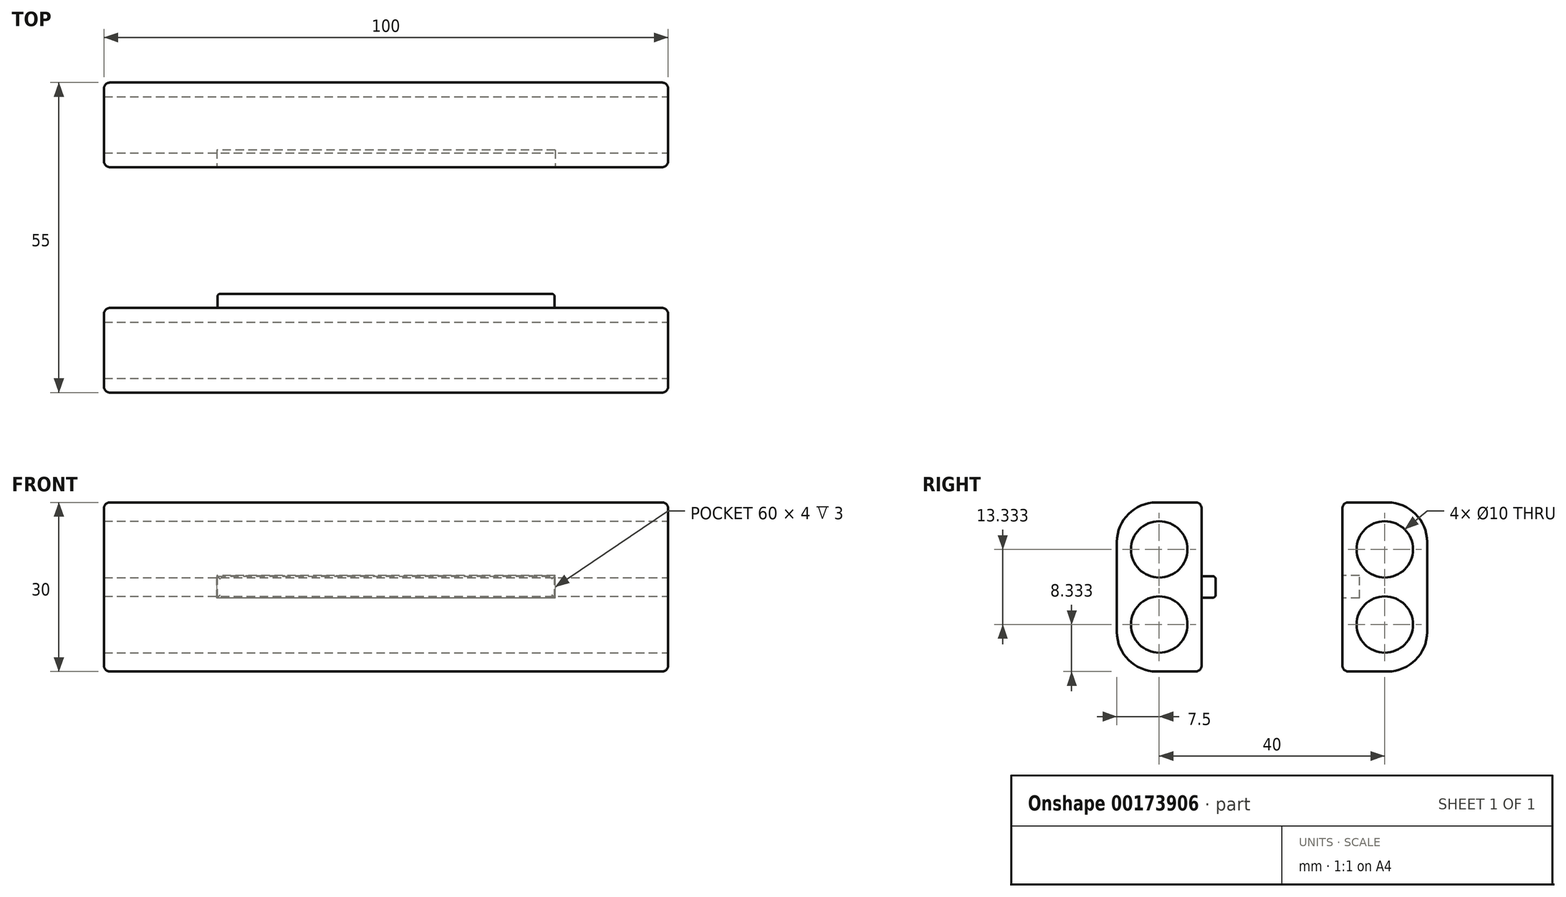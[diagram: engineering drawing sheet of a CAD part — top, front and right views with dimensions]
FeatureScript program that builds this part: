
annotation { "Feature Type Name" : "Feature", "Feature Type Description" : "" }
export const myFeature = defineFeature(function(context is Context, id is Id, definition is map)
    precondition{}
    {
        {
            var Q0;
            Q0=qCreatedBy(makeId("Front.planeOp"),FACE);
            var sketch = newSketch(context, id + "F0", { "sketchPlane" : qUnion([Q0])});
            skLineSegment(sketch, "E0.bottom", {"start": v(50, -15) * mm, "end": v(-50, -15) * mm});
            skLineSegment(sketch, "E0.top", {"start": v(50, 15) * mm, "end": v(-50, 15) * mm});
            skLineSegment(sketch, "E0.left", {"start": v(50, -15) * mm, "end": v(50, 15) * mm});
            skLineSegment(sketch, "E0.right", {"start": v(-50, -15) * mm, "end": v(-50, 15) * mm});
            skPoint(sketch, "E0.middle", {"position": v(0, 0) * mm});
            skSolve(sketch);
        }
        {
            var Q0;
            Q0 = qSketchRegion(id + "F0", true);
            extrude(context, id + "F1", {"entities" : qUnion([Q0]), "oppositeDirection" : true, "depth" : 15 * mm});
        }
        {
            var Q0;
            Q0=makeQuery(id+"F1.opExtrude","SWEPT_FACE",FACE,{"disambiguationData":[OSD([sQuery(id+"F0.wireOp",EDGE,"E0.left")])]});
            var sketch = newSketch(context, id + "F2", { "sketchPlane" : qUnion([Q0])});
            skLineSegment(sketch, "E1", {"start": v(7.5, 15) * mm, "end": v(7.5, -15) * mm, "construction": true});
            skCircle(sketch, "E2", {"center": v(7.5, 6.67) * mm, "radius": 5 * mm});
            skCircle(sketch, "E3", {"center": v(7.5, -6.67) * mm, "radius": 5 * mm});
            skPoint(sketch, "E4.endSnap0", {"position": v(15, 0) * mm});
            skLineSegment(sketch, "E5", {"start": v(7.5, 15) * mm, "end": v(7.5, 11.67) * mm, "construction": true});
            skLineSegment(sketch, "E6", {"start": v(7.5, 1.67) * mm, "end": v(7.5, -1.67) * mm, "construction": true});
            skLineSegment(sketch, "E7", {"start": v(7.5, -11.67) * mm, "end": v(7.5, -15) * mm, "construction": true});
            skSolve(sketch);
        }
        {
            var Q0;
            Q0 = qSketchRegion(id + "F2", true);
            extrude(context, id + "F3", {"entities" : qUnion([Q0]), "operationType" : NewBodyOperationType.REMOVE, "endBound" : BoundingType.THROUGH_ALL, "oppositeDirection" : true, "depth" : 25 * mm});
        }
        {
            var Q0;
            Q0=makeQuery(id+"F1.opExtrude","SWEPT_BODY",BODY,{"disambiguationData":[OSD([sQuery(id+"F0.wireOp",EDGE,"E0.bottom"),sQuery(id+"F0.wireOp",EDGE,"E0.top"),sQuery(id+"F0.wireOp",EDGE,"E0.left"),sQuery(id+"F0.wireOp",EDGE,"E0.right")])]});
            var Q1;
            Q1=makeQuery(id+"F1.opExtrude","CAP_FACE",FACE,{"disambiguationData":[OSD([sQuery(id+"F0.wireOp",EDGE,"E0.bottom"),sQuery(id+"F0.wireOp",EDGE,"E0.top"),sQuery(id+"F0.wireOp",EDGE,"E0.left"),sQuery(id+"F0.wireOp",EDGE,"E0.right")])],"isStart":true});
            mirror(context, id + "F4", {"entities" : qUnion([Q0]), "mirrorPlane" : qUnion([Q1])});
        }
        {
            var Q0;
            Q0=makeQuery(id+"F4.opPattern","COPY",EDGE,{"derivedFrom":makeQuery(id+"F1.opExtrude","CAP_EDGE",EDGE,{"disambiguationData":[OSD([sQuery(id+"F0.wireOp",EDGE,"E0.top")])],"isStart":false}),"instanceName":"1"});
            var Q1;
            Q1=makeQuery(id+"F1.opExtrude","CAP_EDGE",EDGE,{"disambiguationData":[OSD([sQuery(id+"F0.wireOp",EDGE,"E0.top")])],"isStart":false});
            var Q2;
            Q2=makeQuery(id+"F1.opExtrude","CAP_EDGE",EDGE,{"disambiguationData":[OSD([sQuery(id+"F0.wireOp",EDGE,"E0.bottom")])],"isStart":false});
            var Q3;
            Q3=makeQuery(id+"F4.opPattern","COPY",EDGE,{"derivedFrom":makeQuery(id+"F1.opExtrude","CAP_EDGE",EDGE,{"disambiguationData":[OSD([sQuery(id+"F0.wireOp",EDGE,"E0.bottom")])],"isStart":false}),"instanceName":"1"});
            fillet(context, id + "F5", {"entities" : qUnion([Q0, Q1, Q2, Q3]), "radius" : 7 * mm, "tangentPropagation" : true, "allowEdgeOverflow" : false});
        }
        {
            var Q0;
            Q0=makeQuery(id+"F1.opExtrude","CAP_EDGE",EDGE,{"disambiguationData":[OSD([sQuery(id+"F0.wireOp",EDGE,"E0.right")])],"isStart":false});
            var Q1;
            Q1=makeQuery(id+"F4.opPattern","COPY",EDGE,{"derivedFrom":makeQuery(id+"F1.opExtrude","CAP_EDGE",EDGE,{"disambiguationData":[OSD([sQuery(id+"F0.wireOp",EDGE,"E0.right")])],"isStart":false}),"instanceName":"1"});
            var Q2;
            Q2=makeQuery(id+"F4.opPattern","COPY",EDGE,{"derivedFrom":makeQuery(id+"F1.opExtrude","CAP_EDGE",EDGE,{"disambiguationData":[OSD([sQuery(id+"F0.wireOp",EDGE,"E0.left")])],"isStart":false}),"instanceName":"1"});
            var Q3;
            Q3=makeQuery(id+"F1.opExtrude","CAP_EDGE",EDGE,{"disambiguationData":[OSD([sQuery(id+"F0.wireOp",EDGE,"E0.left")])],"isStart":false});
            fillet(context, id + "F6", {"entities" : qUnion([Q0, Q1, Q2, Q3]), "radius" : 1 * mm, "tangentPropagation" : true, "allowEdgeOverflow" : false});
        }
        {
            var Q0;
            Q0=makeQuery(id+"F4.opPattern","COPY",BODY,{"derivedFrom":makeQuery(id+"F1.opExtrude","SWEPT_BODY",BODY,{"disambiguationData":[OSD([sQuery(id+"F0.wireOp",EDGE,"E0.bottom"),sQuery(id+"F0.wireOp",EDGE,"E0.top"),sQuery(id+"F0.wireOp",EDGE,"E0.left"),sQuery(id+"F0.wireOp",EDGE,"E0.right")])]}),"instanceName":"1"});
            var Q1;
            Q1=qCreatedBy(makeId("Front.planeOp"),FACE);
            transform(context, id + "F7", {"entities" : qUnion([Q0]), "transformType" : TransformType.TRANSLATION_DISTANCE, "transformDirection" : qUnion([Q1]), "distance" : 25 * mm, "makeCopy" : false});
        }
        {
            var Q0;
            Q0=makeQuery(id+"F1.opExtrude","CAP_FACE",FACE,{"disambiguationData":[OSD([sQuery(id+"F0.wireOp",EDGE,"E0.bottom"),sQuery(id+"F0.wireOp",EDGE,"E0.top"),sQuery(id+"F0.wireOp",EDGE,"E0.left"),sQuery(id+"F0.wireOp",EDGE,"E0.right")])],"isStart":true});
            var sketch = newSketch(context, id + "F8", { "sketchPlane" : qUnion([Q0])});
            skLineSegment(sketch, "E8.bottom", {"start": v(30, -2) * mm, "end": v(-30, -2) * mm});
            skLineSegment(sketch, "E8.top", {"start": v(30, 2) * mm, "end": v(-30, 2) * mm});
            skLineSegment(sketch, "E8.left", {"start": v(30, -2) * mm, "end": v(30, 2) * mm});
            skLineSegment(sketch, "E8.right", {"start": v(-30, -2) * mm, "end": v(-30, 2) * mm});
            skPoint(sketch, "E8.middle", {"position": v(0, 0) * mm});
            skSolve(sketch);
        }
        {
            var Q0;
            Q0 = qSketchRegion(id + "F8", true);
            extrude(context, id + "F9", {"entities" : qUnion([Q0]), "operationType" : NewBodyOperationType.REMOVE, "oppositeDirection" : true, "depth" : 3 * mm});
        }
        {
            var Q0;
            Q0=makeQuery(id+"F4.opPattern","COPY",FACE,{"derivedFrom":makeQuery(id+"F1.opExtrude","CAP_FACE",FACE,{"disambiguationData":[OSD([sQuery(id+"F0.wireOp",EDGE,"E0.bottom"),sQuery(id+"F0.wireOp",EDGE,"E0.top"),sQuery(id+"F0.wireOp",EDGE,"E0.left"),sQuery(id+"F0.wireOp",EDGE,"E0.right")])],"isStart":true}),"instanceName":"1"});
            var sketch = newSketch(context, id + "F10", { "sketchPlane" : qUnion([Q0])});
            skLineSegment(sketch, "E9.bottom", {"start": v(29.9, -1.9) * mm, "end": v(-29.9, -1.9) * mm});
            skLineSegment(sketch, "E9.top", {"start": v(29.9, 1.9) * mm, "end": v(-29.9, 1.9) * mm});
            skLineSegment(sketch, "E9.left", {"start": v(29.9, -1.9) * mm, "end": v(29.9, 1.9) * mm});
            skLineSegment(sketch, "E9.right", {"start": v(-29.9, -1.9) * mm, "end": v(-29.9, 1.9) * mm});
            skPoint(sketch, "E9.middle", {"position": v(0, 0) * mm});
            skSolve(sketch);
        }
        {
            var Q0;
            Q0 = qSketchRegion(id + "F10", true);
            extrude(context, id + "F11", {"entities" : qUnion([Q0]), "operationType" : NewBodyOperationType.ADD, "depth" : 2.5 * mm});
        }
        {
            var Q0;
            Q0=makeQuery(id+"F11.opExtrude","CAP_EDGE",EDGE,{"disambiguationData":[OSD([sQuery(id+"F10.wireOp",EDGE,"E9.bottom")])],"isStart":false});
            var Q1;
            Q1=makeQuery(id+"F11.opExtrude","CAP_EDGE",EDGE,{"disambiguationData":[OSD([sQuery(id+"F10.wireOp",EDGE,"E9.right")])],"isStart":false});
            var Q2;
            Q2=makeQuery(id+"F11.opExtrude","CAP_EDGE",EDGE,{"disambiguationData":[OSD([sQuery(id+"F10.wireOp",EDGE,"E9.top")])],"isStart":false});
            var Q3;
            Q3=makeQuery(id+"F11.opExtrude","CAP_EDGE",EDGE,{"disambiguationData":[OSD([sQuery(id+"F10.wireOp",EDGE,"E9.left")])],"isStart":false});
            fillet(context, id + "F12", {"entities" : qUnion([Q0, Q1, Q2, Q3]), "radius" : .5 * mm, "tangentPropagation" : true, "allowEdgeOverflow" : false});
        }
        {
            var Q0;
            Q0=makeQuery(id+"F4.opPattern","COPY",EDGE,{"derivedFrom":makeQuery(id+"F1.opExtrude","CAP_EDGE",EDGE,{"disambiguationData":[OSD([sQuery(id+"F0.wireOp",EDGE,"E0.bottom")])],"isStart":true}),"instanceName":"1"});
            fillet(context, id + "F13", {"entities" : qUnion([Q0]), "radius" : 1 * mm, "tangentPropagation" : true, "allowEdgeOverflow" : false});
        }
        {
            var Q0;
            Q0=makeQuery(id+"F1.opExtrude","CAP_EDGE",EDGE,{"disambiguationData":[OSD([sQuery(id+"F0.wireOp",EDGE,"E0.top")])],"isStart":true});
            fillet(context, id + "F14", {"entities" : qUnion([Q0]), "radius" : 1 * mm, "tangentPropagation" : true, "allowEdgeOverflow" : false});
        }
    });
